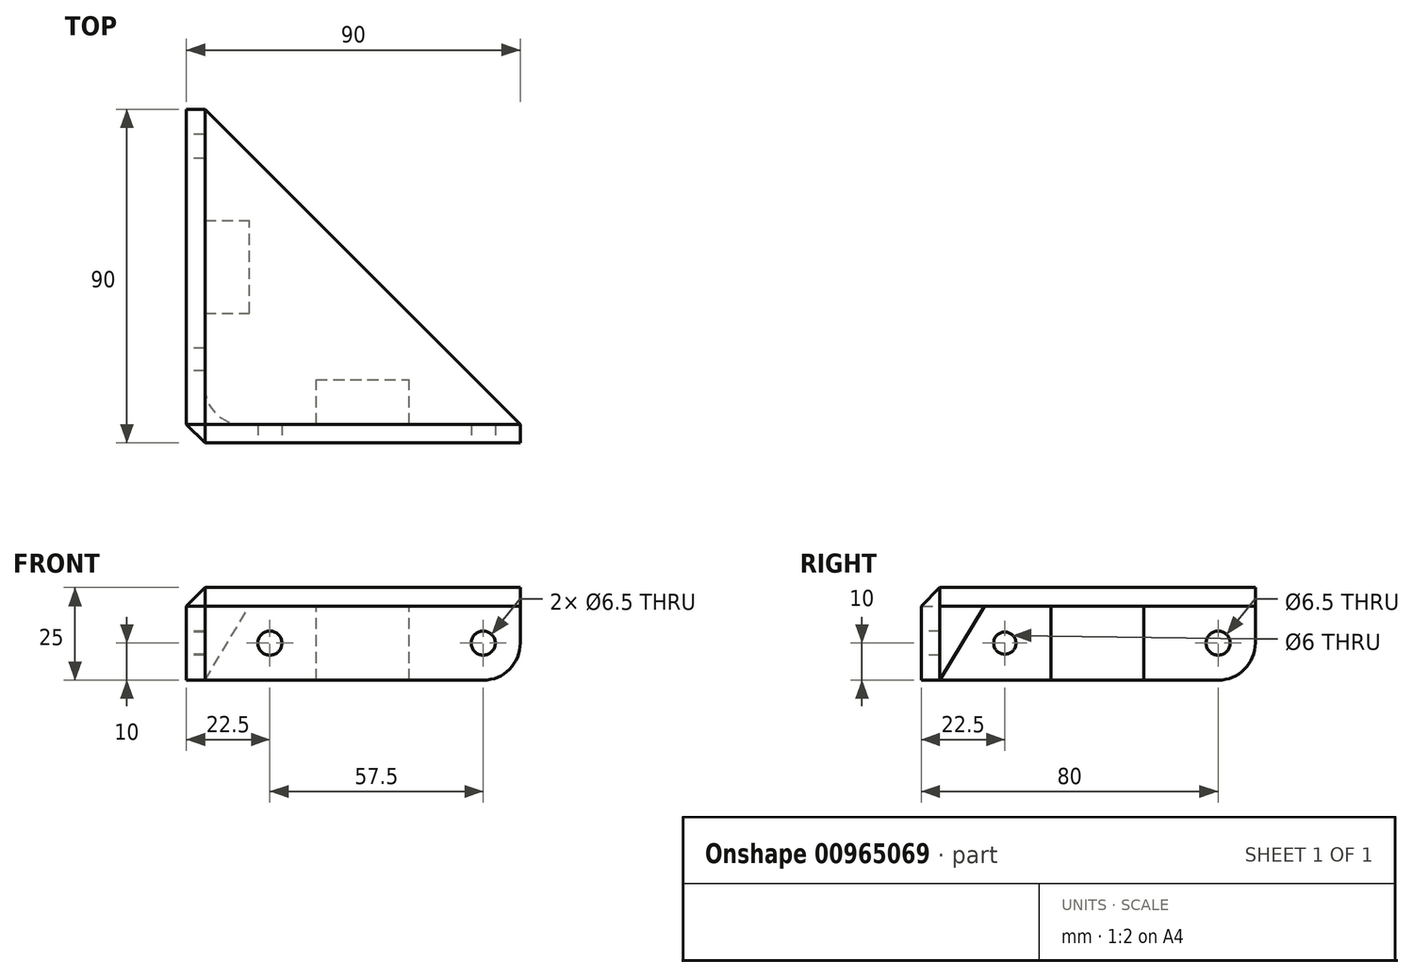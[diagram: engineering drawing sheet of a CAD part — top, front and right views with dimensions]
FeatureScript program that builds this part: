
annotation { "Feature Type Name" : "Feature", "Feature Type Description" : "" }
export const myFeature = defineFeature(function(context is Context, id is Id, definition is map)
    precondition{}
    {
        {
            var Q0;
            Q0=qCreatedBy(makeId("Top.planeOp"),FACE);
            var sketch = newSketch(context, id + "F0", { "sketchPlane" : qUnion([Q0])});
            skLineSegment(sketch, "E0", {"start": v(0, 0) * mm, "end": v(0, 90) * mm});
            skLineSegment(sketch, "E1", {"start": v(90, 0) * mm, "end": v(0, 0) * mm});
            skLineSegment(sketch, "E2", {"start": v(0, 90) * mm, "end": v(5, 90) * mm});
            skLineSegment(sketch, "E3", {"start": v(5, 90) * mm, "end": v(90, 5) * mm});
            skLineSegment(sketch, "E4", {"start": v(90, 5) * mm, "end": v(90, 0) * mm});
            skLineSegment(sketch, "E5", {"start": v(5, 90) * mm, "end": v(5, 5) * mm});
            skLineSegment(sketch, "E6", {"start": v(5, 5) * mm, "end": v(90, 5) * mm});
            skLineSegment(sketch, "E7.bottom", {"start": v(5, 35) * mm, "end": v(17, 35) * mm});
            skLineSegment(sketch, "E7.top", {"start": v(5, 60) * mm, "end": v(17, 60) * mm});
            skLineSegment(sketch, "E7.left", {"start": v(5, 35) * mm, "end": v(5, 60) * mm});
            skLineSegment(sketch, "E7.right", {"start": v(17, 35) * mm, "end": v(17, 60) * mm});
            skLineSegment(sketch, "E8.bottom", {"start": v(35, 5) * mm, "end": v(60, 5) * mm});
            skLineSegment(sketch, "E8.top", {"start": v(35, 17) * mm, "end": v(60, 17) * mm});
            skLineSegment(sketch, "E8.left", {"start": v(35, 5) * mm, "end": v(35, 17) * mm});
            skLineSegment(sketch, "E8.right", {"start": v(60, 5) * mm, "end": v(60, 17) * mm});
            skSolve(sketch);
        }
        {
            var Q0;
            Q0=makeQuery(id+"F0.imprint","IMPRINT",FACE,{"disambiguationData":[TD([[makeQuery(id+"F0.imprint","IMPRINT",EDGE,{"derivedFrom":sQuery(id+"F0.wireOp",EDGE,"E0")}),-1.0]])]});
            var Q1;
            Q1=makeQuery(id+"F0.imprint","IMPRINT",FACE,{"disambiguationData":[TD([[makeQuery(id+"F0.imprint","IMPRINT",EDGE,{"derivedFrom":sQuery(id+"F0.wireOp",EDGE,"E3")}),-1.0]])]});
            var Q2;
            {var subQ2=sQuery(id+"F0.wireOp",EDGE,"E7.bottom");Q2=makeQuery(id+"F0.imprint","IMPRINT",FACE,{"disambiguationData":[TD([[makeQuery(id+"F0.imprint","IMPRINT",EDGE,{"derivedFrom":subQ2}),1.0]])]});}
            var Q3;
            Q3=makeQuery(id+"F0.imprint","IMPRINT",FACE,{"disambiguationData":[TD([[makeQuery(id+"F0.imprint","IMPRINT",EDGE,{"derivedFrom":sQuery(id+"F0.wireOp",EDGE,"E8.top")}),-1.0]])]});
            extrude(context, id + "F1", {"entities" : qUnion([Q0, Q1, Q2, Q3]), "depth" : 5 * mm, "offsetDistance" : 25 * mm});
        }
        {
            var Q0;
            Q0=makeQuery(id+"F0.imprint","IMPRINT",FACE,{"disambiguationData":[TD([[makeQuery(id+"F0.imprint","IMPRINT",EDGE,{"derivedFrom":sQuery(id+"F0.wireOp",EDGE,"E0")}),-1.0]])]});
            var Q1;
            {var subQ2=sQuery(id+"F0.wireOp",EDGE,"E7.bottom");Q1=makeQuery(id+"F0.imprint","IMPRINT",FACE,{"disambiguationData":[TD([[makeQuery(id+"F0.imprint","IMPRINT",EDGE,{"derivedFrom":subQ2}),1.0]])]});}
            var Q2;
            Q2=makeQuery(id+"F0.imprint","IMPRINT",FACE,{"disambiguationData":[TD([[makeQuery(id+"F0.imprint","IMPRINT",EDGE,{"derivedFrom":sQuery(id+"F0.wireOp",EDGE,"E8.top")}),-1.0]])]});
            extrude(context, id + "F2", {"entities" : qUnion([Q0, Q1, Q2]), "operationType" : NewBodyOperationType.ADD, "oppositeDirection" : true, "depth" : 20 * mm, "offsetDistance" : 25 * mm});
        }
        {
            var Q0;
            Q0=makeQuery(id+"F2.opExtrude","SWEPT_EDGE",EDGE,{"disambiguationData":[OSD([sQuery(id+"F0.wireOp",EDGE,"E5"),sQuery(id+"F0.wireOp",EDGE,"E6")])]});
            var Q1;
            Q1=makeQuery(id+"F2.opExtrude","CAP_EDGE",EDGE,{"disambiguationData":[OSD([sQuery(id+"F0.wireOp",EDGE,"E2")])],"isStart":false});
            var Q2;
            Q2=makeQuery(id+"F2.opExtrude","CAP_EDGE",EDGE,{"disambiguationData":[OSD([sQuery(id+"F0.wireOp",EDGE,"E4")])],"isStart":false});
            fillet(context, id + "F3", {"entities" : qUnion([Q0, Q1, Q2]), "tangentPropagation" : true, "radius" : 10 * mm, "defaultsChanged" : false, "vertexSettings" : [], "allowEdgeOverflow" : false});
        }
        {
            var Q0;
            {var subQ0=sQuery(id+"F0.wireOp",EDGE,"E0");Q0=makeQuery(id+"F2.boolean.opBoolean","MERGE",FACE,{"derivedFrom":[makeQuery(id+"F1.opExtrude","SWEPT_FACE",FACE,{"disambiguationData":[OSD([subQ0])]}),makeQuery(id+"F2.opExtrude","SWEPT_FACE",FACE,{"disambiguationData":[OSD([subQ0])]})]});}
            var sketch = newSketch(context, id + "F4", { "sketchPlane" : qUnion([Q0])});
            skCircle(sketch, "E9", {"center": v(-80, -10) * mm, "radius": 3.25 * mm});
            skCircle(sketch, "E10", {"center": v(-22.5, -10) * mm, "radius": 3 * mm});
            skSolve(sketch);
        }
        {
            var Q0;
            {var subQ0=sQuery(id+"F0.wireOp",EDGE,"E1");Q0=makeQuery(id+"F2.boolean.opBoolean","MERGE",FACE,{"derivedFrom":[makeQuery(id+"F1.opExtrude","SWEPT_FACE",FACE,{"disambiguationData":[OSD([subQ0])]}),makeQuery(id+"F2.opExtrude","SWEPT_FACE",FACE,{"disambiguationData":[OSD([subQ0])]})]});}
            var sketch = newSketch(context, id + "F5", { "sketchPlane" : qUnion([Q0])});
            skCircle(sketch, "E11", {"center": v(22.5, -10) * mm, "radius": 3.25 * mm});
            skCircle(sketch, "E12", {"center": v(80, -10) * mm, "radius": 3.25 * mm});
            skSolve(sketch);
        }
        {
            var Q0;
            Q0=makeQuery(id+"F5.imprint","IMPRINT",FACE,{"disambiguationData":[TD([[makeQuery(id+"F5.imprint","IMPRINT",EDGE,{"derivedFrom":sQuery(id+"F5.wireOp",EDGE,"E11")}),1.0]])]});
            var Q1;
            Q1=makeQuery(id+"F5.imprint","IMPRINT",FACE,{"disambiguationData":[TD([[makeQuery(id+"F5.imprint","IMPRINT",EDGE,{"derivedFrom":sQuery(id+"F5.wireOp",EDGE,"E12")}),1.0]])]});
            extrude(context, id + "F6", {"entities" : qUnion([Q0, Q1]), "operationType" : NewBodyOperationType.REMOVE, "oppositeDirection" : true, "depth" : 25 * mm, "offsetDistance" : 25 * mm});
        }
        {
            var Q0;
            Q0=makeQuery(id+"F4.imprint","IMPRINT",FACE,{"disambiguationData":[TD([[makeQuery(id+"F4.imprint","IMPRINT",EDGE,{"derivedFrom":sQuery(id+"F4.wireOp",EDGE,"E10")}),1.0]])]});
            var Q1;
            Q1=makeQuery(id+"F4.imprint","IMPRINT",FACE,{"disambiguationData":[TD([[makeQuery(id+"F4.imprint","IMPRINT",EDGE,{"derivedFrom":sQuery(id+"F4.wireOp",EDGE,"E9")}),1.0]])]});
            extrude(context, id + "F7", {"entities" : qUnion([Q0, Q1]), "operationType" : NewBodyOperationType.REMOVE, "oppositeDirection" : true, "depth" : 25 * mm, "offsetDistance" : 25 * mm});
        }
        {
            var Q0;
            Q0=makeQuery(id+"F2.opExtrude","CAP_EDGE",EDGE,{"disambiguationData":[OSD([sQuery(id+"F0.wireOp",EDGE,"E7.right")])],"isStart":false});
            var Q1;
            Q1=makeQuery(id+"F2.opExtrude","CAP_EDGE",EDGE,{"disambiguationData":[OSD([sQuery(id+"F0.wireOp",EDGE,"E8.top")])],"isStart":false});
            chamfer(context, id + "F8", {"entities" : qUnion([Q0, Q1]), "chamferType" : ChamferType.TWO_OFFSETS, "width1" : 20 * mm, "oppositeDirection" : false, "width2" : 12 * mm, "tangentPropagation" : true});
        }
        {
            var Q0;
            {var subQ0=sQuery(id+"F0.wireOp",EDGE,"E1");var subQ1=sQuery(id+"F0.wireOp",EDGE,"E0");Q0=makeQuery(id+"F2.boolean.opBoolean","MERGE",EDGE,{"derivedFrom":[makeQuery(id+"F1.opExtrude","SWEPT_EDGE",EDGE,{"disambiguationData":[OSD([subQ1,subQ0])]}),makeQuery(id+"F2.opExtrude","SWEPT_EDGE",EDGE,{"disambiguationData":[OSD([subQ1,subQ0])]})]});}
            var Q1;
            Q1=makeQuery(id+"F1.opExtrude","CAP_EDGE",EDGE,{"disambiguationData":[OSD([sQuery(id+"F0.wireOp",EDGE,"E1")])],"isStart":false});
            var Q2;
            Q2=makeQuery(id+"F1.opExtrude","CAP_EDGE",EDGE,{"disambiguationData":[OSD([sQuery(id+"F0.wireOp",EDGE,"E0")])],"isStart":false});
            chamfer(context, id + "F9", {"entities" : qUnion([Q0, Q1, Q2]), "width" : 5 * mm, "tangentPropagation" : true});
        }
    });
